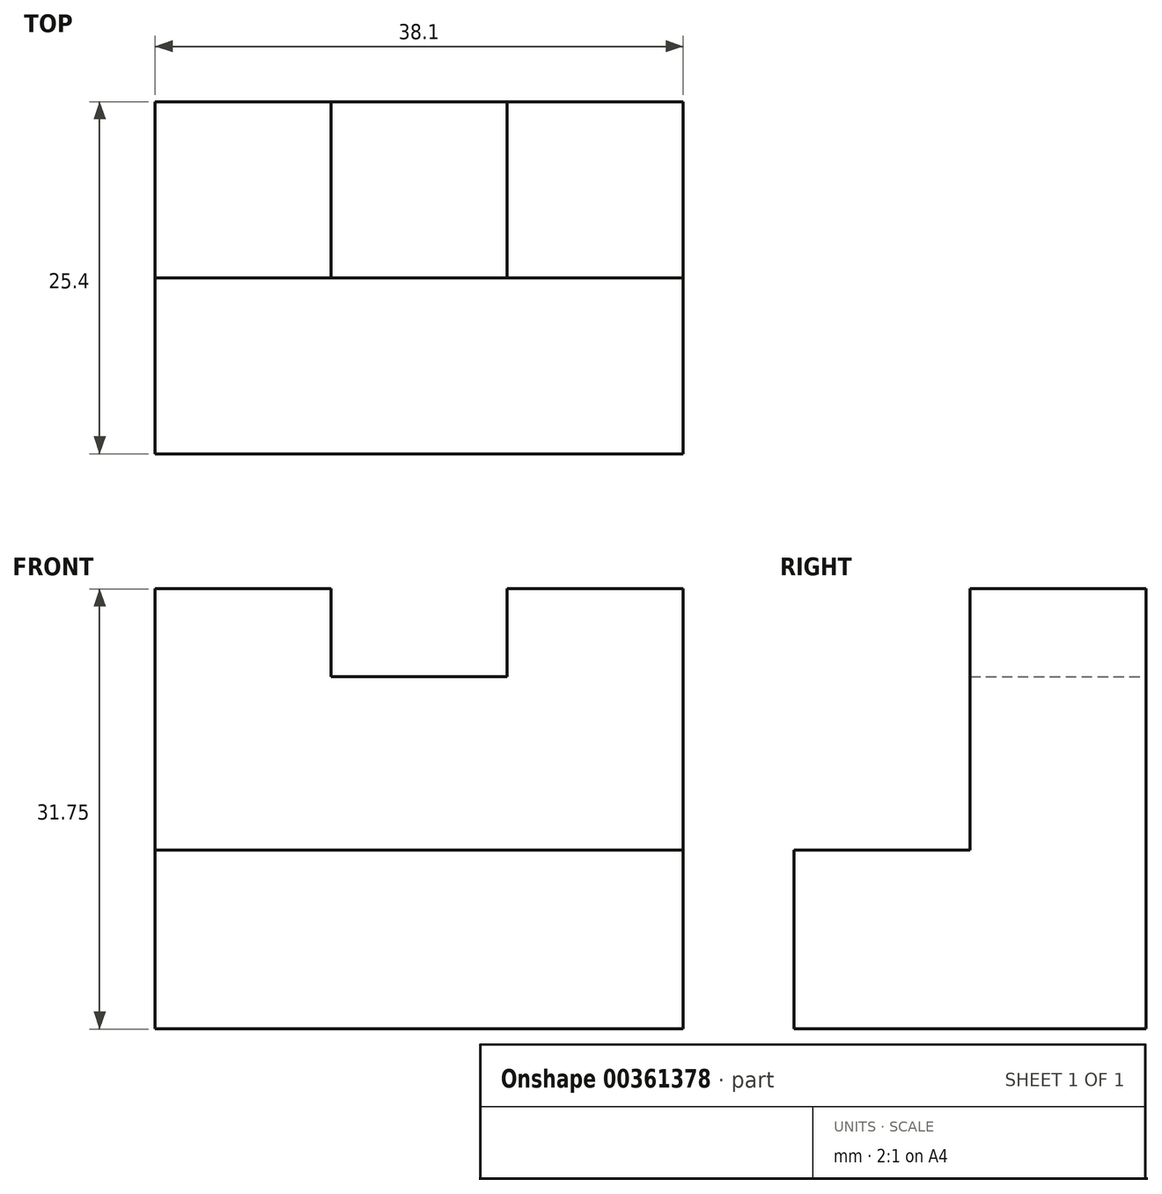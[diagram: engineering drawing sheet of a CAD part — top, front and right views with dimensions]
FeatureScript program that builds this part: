
annotation { "Feature Type Name" : "Feature", "Feature Type Description" : "" }
export const myFeature = defineFeature(function(context is Context, id is Id, definition is map)
    precondition{}
    {
        {
            var Q0;
            Q0=qCreatedBy(makeId("Front.planeOp"),FACE);
            var sketch = newSketch(context, id + "F0", { "sketchPlane" : qUnion([Q0])});
            skLineSegment(sketch, "E0", {"start": v(-35.62, 18.83) * mm, "end": v(-22.92, 18.83) * mm});
            skLineSegment(sketch, "E1", {"start": v(-22.92, 18.83) * mm, "end": v(-22.92, 12.48) * mm});
            skLineSegment(sketch, "E2", {"start": v(-22.92, 12.48) * mm, "end": v(-10.22, 12.48) * mm});
            skLineSegment(sketch, "E3", {"start": v(-10.22, 12.48) * mm, "end": v(-10.22, 18.83) * mm});
            skLineSegment(sketch, "E4", {"start": v(-10.22, 18.83) * mm, "end": v(2.48, 18.83) * mm});
            skLineSegment(sketch, "E5", {"start": v(2.48, 18.83) * mm, "end": v(2.48, -12.92) * mm});
            skLineSegment(sketch, "E6", {"start": v(2.48, -12.92) * mm, "end": v(-35.62, -12.92) * mm});
            skLineSegment(sketch, "E7", {"start": v(-35.62, -12.92) * mm, "end": v(-35.62, 18.83) * mm});
            skSolve(sketch);
        }
        {
            var Q0;
            Q0 = qSketchRegion(id + "F0", true);
            extrude(context, id + "F1", {"entities" : qUnion([Q0]), "depth" : 12.7 * mm});
        }
        {
            var Q0;
            Q0=makeQuery(id+"F1.opExtrude","CAP_FACE",FACE,{"disambiguationData":[OSD([sQuery(id+"F0.wireOp",EDGE,"E0"),sQuery(id+"F0.wireOp",EDGE,"E1"),sQuery(id+"F0.wireOp",EDGE,"E2"),sQuery(id+"F0.wireOp",EDGE,"E3"),sQuery(id+"F0.wireOp",EDGE,"E4"),sQuery(id+"F0.wireOp",EDGE,"E5"),sQuery(id+"F0.wireOp",EDGE,"E6"),sQuery(id+"F0.wireOp",EDGE,"E7")])],"isStart":false});
            var sketch = newSketch(context, id + "F2", { "sketchPlane" : qUnion([Q0])});
            skLineSegment(sketch, "E8", {"start": v(-35.62, 0) * mm, "end": v(2.48, 0) * mm});
            skSolve(sketch);
        }
        {
            var Q0;
            {var subQ0=sQuery(id+"F2.wireOp",EDGE,"E8");Q0=makeQuery(id+"F2.imprint","IMPRINT",FACE,{"disambiguationData":[TD([[makeQuery(id+"F2.imprint","IMPRINT",EDGE,{"derivedFrom":subQ0}),-1.0]])]});}
            extrude(context, id + "F3", {"entities" : qUnion([Q0]), "operationType" : NewBodyOperationType.ADD, "depth" : 12.7 * mm});
        }
    });
